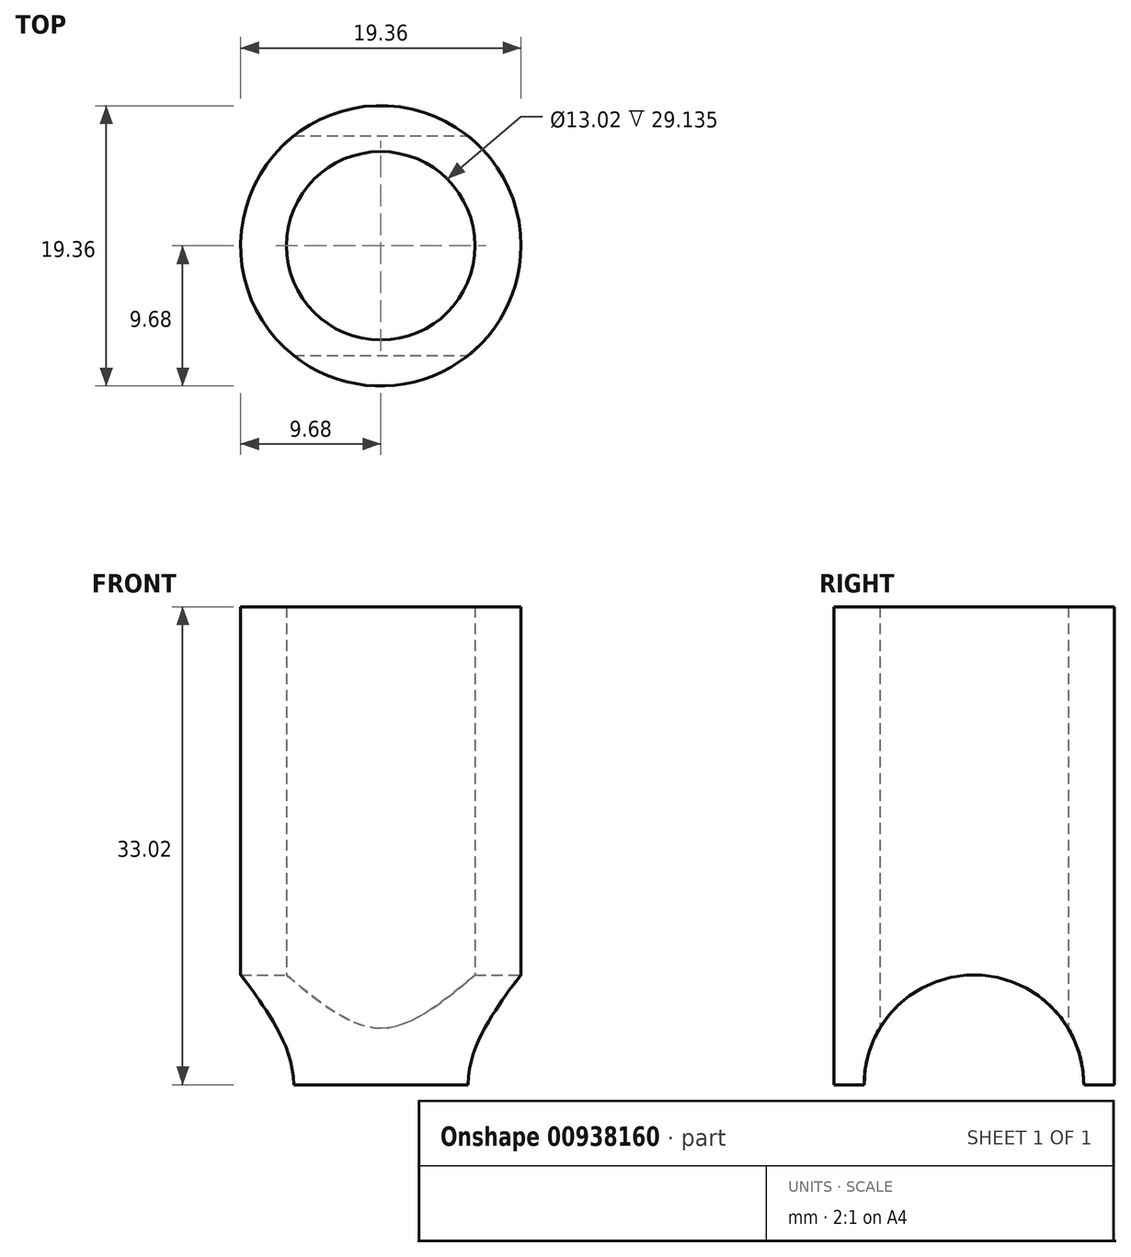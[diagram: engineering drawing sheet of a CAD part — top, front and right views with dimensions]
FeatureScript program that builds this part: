
annotation { "Feature Type Name" : "Feature", "Feature Type Description" : "" }
export const myFeature = defineFeature(function(context is Context, id is Id, definition is map)
    precondition{}
    {
        {
            var Q0;
            Q0=qCreatedBy(makeId("Top.planeOp"),FACE);
            var sketch = newSketch(context, id + "F0", { "sketchPlane" : qUnion([Q0])});
            skCircle(sketch, "E0", {"center": v(0, 0) * mm, "radius": 6.5 * mm});
            skCircle(sketch, "E1", {"center": v(0, 0) * mm, "radius": 9.68 * mm});
            skSolve(sketch);
        }
        {
            var Q0;
            Q0=makeQuery(id+"F0.imprint","IMPRINT",FACE,{"disambiguationData":[TD([[makeQuery(id+"F0.imprint","IMPRINT",EDGE,{"derivedFrom":sQuery(id+"F0.wireOp",EDGE,"E0")}),-1.0]])]});
            extrude(context, id + "F1", {"entities" : qUnion([Q0]), "depth" : 33.02 * mm, "offsetDistance" : 25 * mm});
        }
        {
            var Q0;
            Q0=qCreatedBy(makeId("Right.planeOp"),FACE);
            var sketch = newSketch(context, id + "F2", { "sketchPlane" : qUnion([Q0])});
            skArc(sketch, "E2", {"start": v(-7.59, 0) * mm, "mid": v(0, 7.59) * mm, "end": v(7.59, 0) * mm});
            skLineSegment(sketch, "E3", {"start": v(-7.59, 0) * mm, "end": v(7.59, 0) * mm});
            skSolve(sketch);
        }
        {
            var Q0;
            Q0 = qSketchRegion(id + "F2", true);
            extrude(context, id + "F3", {"entities" : qUnion([Q0]), "operationType" : NewBodyOperationType.REMOVE, "oppositeDirection" : true, "depth" : 25 * mm, "offsetDistance" : 25 * mm});
        }
        {
            var Q0;
            Q0 = qSketchRegion(id + "F2", true);
            extrude(context, id + "F4", {"entities" : qUnion([Q0]), "operationType" : NewBodyOperationType.REMOVE, "depth" : 54.6 * mm, "offsetDistance" : 25 * mm});
        }
    });
